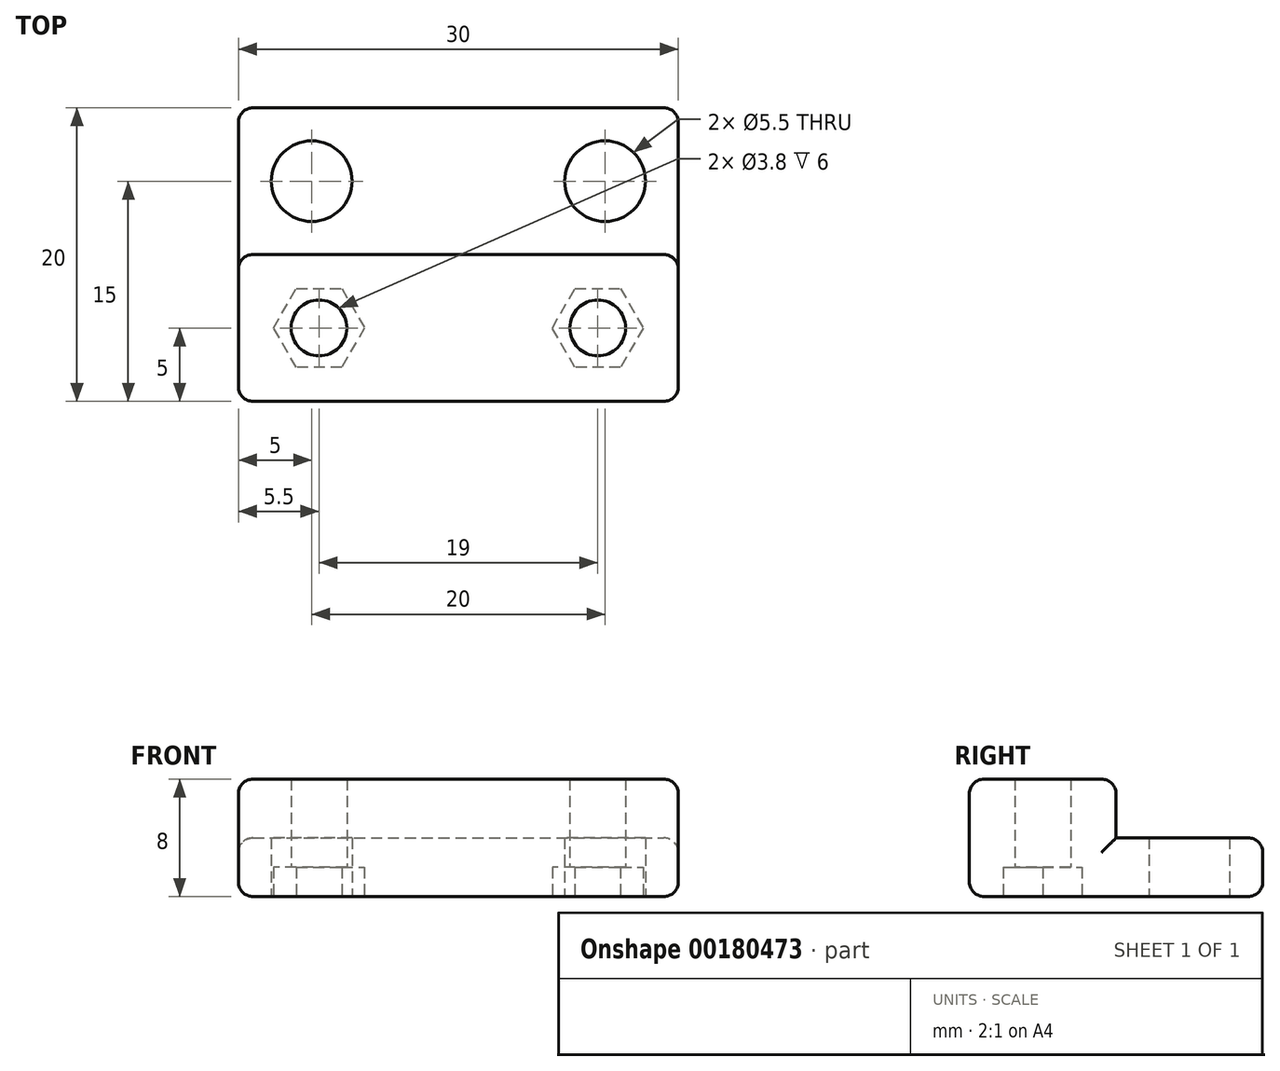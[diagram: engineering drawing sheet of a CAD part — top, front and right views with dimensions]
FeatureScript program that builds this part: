
annotation { "Feature Type Name" : "Feature", "Feature Type Description" : "" }
export const myFeature = defineFeature(function(context is Context, id is Id, definition is map)
    precondition{}
    {
        {
            var Q0;
            Q0=qCreatedBy(makeId("Top.planeOp"),FACE);
            var sketch = newSketch(context, id + "F0", { "sketchPlane" : qUnion([Q0])});
            skLineSegment(sketch, "E0.bottom", {"start": v(0, 0) * mm, "end": v(30, 0) * mm});
            skLineSegment(sketch, "E0.top", {"start": v(0, 20) * mm, "end": v(30, 20) * mm});
            skLineSegment(sketch, "E0.left", {"start": v(0, 0) * mm, "end": v(0, 20) * mm});
            skLineSegment(sketch, "E0.right", {"start": v(30, 0) * mm, "end": v(30, 20) * mm});
            skCircle(sketch, "E1", {"center": v(5, 15) * mm, "radius": 2.75 * mm});
            skCircle(sketch, "E2", {"center": v(25, 15) * mm, "radius": 2.75 * mm});
            skLineSegment(sketch, "E3", {"start": v(0, 10) * mm, "end": v(30, 10) * mm});
            skCircle(sketch, "E4", {"center": v(5.5, 5) * mm, "radius": 1.9 * mm});
            skCircle(sketch, "E5", {"center": v(24.5, 5) * mm, "radius": 1.9 * mm});
            skCircle(sketch, "E6.cCircle", {"center": v(5.5, 5) * mm, "radius": 3.1 * mm, "construction": true});
            skLineSegment(sketch, "E6.0", {"start": v(2.4, 5) * mm, "end": v(3.95, 7.68) * mm});
            skLineSegment(sketch, "E6.1", {"start": v(3.95, 7.68) * mm, "end": v(7.05, 7.68) * mm});
            skLineSegment(sketch, "E6.2", {"start": v(7.05, 7.68) * mm, "end": v(8.6, 5) * mm});
            skLineSegment(sketch, "E6.3", {"start": v(8.6, 5) * mm, "end": v(7.05, 2.32) * mm});
            skLineSegment(sketch, "E6.4", {"start": v(7.05, 2.32) * mm, "end": v(3.95, 2.32) * mm});
            skLineSegment(sketch, "E6.5", {"start": v(3.95, 2.32) * mm, "end": v(2.4, 5) * mm});
            skCircle(sketch, "E7.cCircle", {"center": v(24.5, 5) * mm, "radius": 3.1 * mm, "construction": true});
            skLineSegment(sketch, "E7.0", {"start": v(21.4, 5) * mm, "end": v(22.95, 7.68) * mm});
            skLineSegment(sketch, "E7.1", {"start": v(22.95, 7.68) * mm, "end": v(26.05, 7.68) * mm});
            skLineSegment(sketch, "E7.2", {"start": v(26.05, 7.68) * mm, "end": v(27.6, 5) * mm});
            skLineSegment(sketch, "E7.3", {"start": v(27.6, 5) * mm, "end": v(26.05, 2.32) * mm});
            skLineSegment(sketch, "E7.4", {"start": v(26.05, 2.32) * mm, "end": v(22.95, 2.32) * mm});
            skLineSegment(sketch, "E7.5", {"start": v(22.95, 2.32) * mm, "end": v(21.4, 5) * mm});
            skSolve(sketch);
        }
        {
            var Q0;
            {var subQ1=sQuery(id+"F0.wireOp",EDGE,"E0.top");Q0=makeQuery(id+"F0.imprint","IMPRINT",FACE,{"disambiguationData":[TD([[makeQuery(id+"F0.imprint","IMPRINT",EDGE,{"derivedFrom":subQ1}),-1.0]])]});}
            extrude(context, id + "F1", {"entities" : qUnion([Q0]), "depth" : 4 * mm});
        }
        {
            var Q0;
            {var subQ1=sQuery(id+"F0.wireOp",EDGE,"E0.bottom");Q0=makeQuery(id+"F0.imprint","IMPRINT",FACE,{"disambiguationData":[TD([[makeQuery(id+"F0.imprint","IMPRINT",EDGE,{"derivedFrom":subQ1}),1.0]])]});}
            extrude(context, id + "F2", {"entities" : qUnion([Q0]), "operationType" : NewBodyOperationType.ADD, "depth" : 8 * mm});
        }
        {
            var Q0;
            Q0=makeQuery(id+"F0.imprint","IMPRINT",FACE,{"disambiguationData":[TD([[makeQuery(id+"F0.imprint","IMPRINT",EDGE,{"derivedFrom":sQuery(id+"F0.wireOp",EDGE,"E4")}),-1.0]])]});
            var Q1;
            Q1=makeQuery(id+"F0.imprint","IMPRINT",FACE,{"disambiguationData":[TD([[makeQuery(id+"F0.imprint","IMPRINT",EDGE,{"derivedFrom":sQuery(id+"F0.wireOp",EDGE,"E5")}),-1.0]])]});
            extrude(context, id + "F3", {"entities" : qUnion([Q0, Q1]), "operationType" : NewBodyOperationType.ADD, "depth" : 8 * mm, "hasSecondDirection" : true, "secondDirectionOppositeDirection" : false, "secondDirectionDepth" : 2 * mm});
        }
        {
            var Q0;
            Q0=makeQuery(id+"F2.opExtrude","CAP_EDGE",EDGE,{"disambiguationData":[OSD([sQuery(id+"F0.wireOp",EDGE,"E0.left")])],"isStart":false});
            var Q1;
            Q1=makeQuery(id+"F2.opExtrude","CAP_EDGE",EDGE,{"disambiguationData":[OSD([sQuery(id+"F0.wireOp",EDGE,"E0.bottom")])],"isStart":false});
            var Q2;
            Q2=makeQuery(id+"F2.opExtrude","CAP_EDGE",EDGE,{"disambiguationData":[OSD([sQuery(id+"F0.wireOp",EDGE,"E0.right")])],"isStart":false});
            var Q3;
            Q3=makeQuery(id+"F2.opExtrude","CAP_EDGE",EDGE,{"disambiguationData":[OSD([sQuery(id+"F0.wireOp",EDGE,"E3")])],"isStart":false});
            var Q4;
            Q4=makeQuery(id+"F1.opExtrude","CAP_EDGE",EDGE,{"disambiguationData":[OSD([sQuery(id+"F0.wireOp",EDGE,"E3")])],"isStart":false});
            var Q5;
            Q5=makeQuery(id+"F1.opExtrude","CAP_EDGE",EDGE,{"disambiguationData":[OSD([sQuery(id+"F0.wireOp",EDGE,"E0.top")])],"isStart":false});
            var Q6;
            Q6=makeQuery(id+"F1.opExtrude","CAP_EDGE",EDGE,{"disambiguationData":[OSD([sQuery(id+"F0.wireOp",EDGE,"E0.left")])],"isStart":false});
            var Q7;
            Q7=makeQuery(id+"F1.opExtrude","CAP_EDGE",EDGE,{"disambiguationData":[OSD([sQuery(id+"F0.wireOp",EDGE,"E0.right")])],"isStart":false});
            var Q8;
            Q8=makeQuery(id+"F2.opExtrude","SWEPT_EDGE",EDGE,{"disambiguationData":[OSD([sQuery(id+"F0.wireOp",EDGE,"E0.left"),sQuery(id+"F0.wireOp",EDGE,"E3")])]});
            var Q9;
            Q9=makeQuery(id+"F2.opExtrude","SWEPT_EDGE",EDGE,{"disambiguationData":[OSD([sQuery(id+"F0.wireOp",EDGE,"E0.right"),sQuery(id+"F0.wireOp",EDGE,"E3")])]});
            var Q10;
            Q10=makeQuery(id+"F2.opExtrude","SWEPT_EDGE",EDGE,{"disambiguationData":[OSD([sQuery(id+"F0.wireOp",EDGE,"E0.bottom"),sQuery(id+"F0.wireOp",EDGE,"E0.left")])]});
            var Q11;
            {var subQ0=sQuery(id+"F0.wireOp",EDGE,"E0.left");Q11=makeQuery(id+"F2.boolean.opBoolean","MERGE",EDGE,{"derivedFrom":[makeQuery(id+"F1.opExtrude","CAP_EDGE",EDGE,{"disambiguationData":[OSD([subQ0])],"isStart":true}),makeQuery(id+"F2.opExtrude","CAP_EDGE",EDGE,{"disambiguationData":[OSD([subQ0])],"isStart":true})]});}
            var Q12;
            Q12=makeQuery(id+"F1.opExtrude","SWEPT_EDGE",EDGE,{"disambiguationData":[OSD([sQuery(id+"F0.wireOp",EDGE,"E0.top"),sQuery(id+"F0.wireOp",EDGE,"E0.left")])]});
            var Q13;
            Q13=makeQuery(id+"F1.opExtrude","CAP_EDGE",EDGE,{"disambiguationData":[OSD([sQuery(id+"F0.wireOp",EDGE,"E0.top")])],"isStart":true});
            var Q14;
            Q14=makeQuery(id+"F1.opExtrude","SWEPT_EDGE",EDGE,{"disambiguationData":[OSD([sQuery(id+"F0.wireOp",EDGE,"E0.top"),sQuery(id+"F0.wireOp",EDGE,"E0.right")])]});
            var Q15;
            {var subQ0=sQuery(id+"F0.wireOp",EDGE,"E0.right");Q15=makeQuery(id+"F2.boolean.opBoolean","MERGE",EDGE,{"derivedFrom":[makeQuery(id+"F1.opExtrude","CAP_EDGE",EDGE,{"disambiguationData":[OSD([subQ0])],"isStart":true}),makeQuery(id+"F2.opExtrude","CAP_EDGE",EDGE,{"disambiguationData":[OSD([subQ0])],"isStart":true})]});}
            var Q16;
            Q16=makeQuery(id+"F2.opExtrude","SWEPT_EDGE",EDGE,{"disambiguationData":[OSD([sQuery(id+"F0.wireOp",EDGE,"E0.bottom"),sQuery(id+"F0.wireOp",EDGE,"E0.right")])]});
            var Q17;
            Q17=makeQuery(id+"F2.opExtrude","CAP_EDGE",EDGE,{"disambiguationData":[OSD([sQuery(id+"F0.wireOp",EDGE,"E0.bottom")])],"isStart":true});
            fillet(context, id + "F4", {"entities" : qUnion([Q0, Q1, Q2, Q3, Q4, Q5, Q6, Q7, Q8, Q9, Q10, Q11, Q12, Q13, Q14, Q15, Q16, Q17]), "radius" : 1 * mm, "tangentPropagation" : true, "allowEdgeOverflow" : false});
        }
    });
